# Revit family: Electronics_Visual-TVs_ViewSonic_ViewSonicR-CDE4320-4K-Ultra-HD-commercia
name_source: partatom
category: Electrical Equipment
revit_build: Autodesk Revit 2017 (Build: 20190508_0315(x64)
units: mm (PartAtom-declared; Revit-internal decimal feet)

## family parameters
Always vertical = Yes
Cut with Voids When Loaded = No
OmniClass Number = 23.80.00.00
OmniClass Title = Electric Power and Lighting
Panel Configuration = Two Columns, Circuits Across
Part Type = Panelboard
Room Calculation Point = No
Round Connector Dimension = Use Diameter
Shared = No
Work Plane-Based = No

## types (1)
- CDE 4320
    Aspect Ratio = 3840 x 2160
    Assembly Code = D5030500
    Backlight = WLED
    Backlight Life = 40,000 Hours Typ
    Bezel = Slim
    Brightness = 350 nits (typ.)
    Colors = 1.07B colors
    Contrast Ratio = 1100:1 Typ.
    Cover Material = Plastic - ViewSonic - Black
    Covering Color = Plastic - ViewSonic - Black
    Description = The ViewSonic® CDE4320 is a 43’’ (42.51” viewable) 4K Ultra HD commercial display purpose-built to deliver eye-catching imagery for hotels, restaurants, retail, business, and more. With stunning 3840x2160 resolution, 350-nit high brightness, wide viewing angles, and dual 10W speakers, this display provides immersive, high-impact messaging wherever needed. In addition to HDMI and DVI inputs to connect with various high definition devices, this display utilizes an integrated multi-core processor and 16GB of internal memory, allowing customers to playback multimedia content via USB without the need for a PC. To make life even easier, the bundled vController software offers easy maintenance and intuitive interfaces for remote management via a PC server or laptop, and its flicker-free and blue light filter technologies help provide a comfortable viewing environment.
    Display Area (mm) = 41.184 (H) x 529.416 (V) (42.51” diagonal)
    Display Size = 43"
    Edition number = 1
    Hardness = 3H
    Keynote = 11130
    Light Source = DLED
    Manufacturer = ViewSonic
    Model = cde4320
    Native Resolution = 3840x2160
    Orientation = Landscape
    Panel Size = 43"
    Product Guid = 04618ea5-7388-44f0-a38c-e1773508592f
    Product data url = https://www.bimobject.com
    Resolution = 3840x2160; 16:9
    Response Time = 6 ms
    Screen Material = Screen - ViewSonic - CDE4320
    Surface Treatment = Anti-Glare, 2H, Haze 3%
    Type/ Tech = TFT LCD Module. IPS type, DLED backlight
    URL = https://www.viewsonic.com
    Viewable Area (In.) = 43"
    Viewing Angles = H = 178, V = 178 typ

## geometry (parser evidence)
native form markers: Sweep x2
no freeform markers — native parametric forms only
